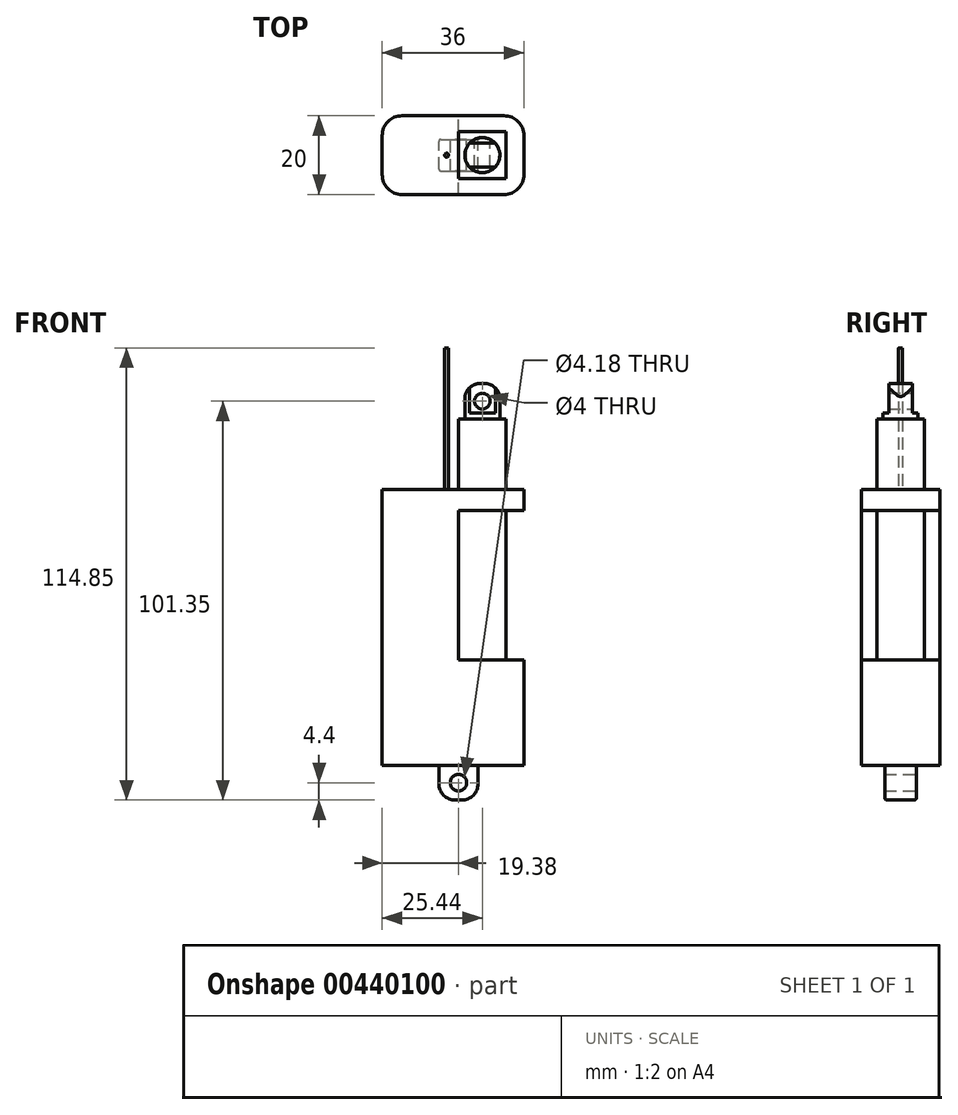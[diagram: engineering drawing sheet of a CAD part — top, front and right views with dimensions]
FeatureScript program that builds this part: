
annotation { "Feature Type Name" : "Feature", "Feature Type Description" : "" }
export const myFeature = defineFeature(function(context is Context, id is Id, definition is map)
    precondition{}
    {
        {
            var Q0;
            Q0=qCreatedBy(makeId("Front.planeOp"),FACE);
            var sketch = newSketch(context, id + "F0", { "sketchPlane" : qUnion([Q0])});
            skLineSegment(sketch, "E0", {"start": v(0, 0) * mm, "end": v(0, 70.05) * mm, "construction": true});
            skLineSegment(sketch, "E1", {"start": v(0, 0) * mm, "end": v(0, -8.8) * mm, "construction": true});
            skCircle(sketch, "E2", {"center": v(0, -4.4) * mm, "radius": 2.09 * mm});
            skLineSegment(sketch, "E3", {"start": v(-4.98, 0) * mm, "end": v(-4.98, -4.62) * mm});
            skLineSegment(sketch, "E4", {"start": v(-0.8, -8.8) * mm, "end": v(0.8, -8.8) * mm});
            skLineSegment(sketch, "E5", {"start": v(4.98, -4.62) * mm, "end": v(4.98, 0) * mm});
            skPoint(sketch, "E6.visualSharp", {"position": v(-4.98, -8.8) * mm});
            skArc(sketch, "E6.filletArc", {"start": v(-4.98, -4.62) * mm, "mid": v(-3.76, -7.58) * mm, "end": v(-0.8, -8.8) * mm});
            skPoint(sketch, "E7.visualSharp", {"position": v(4.98, -8.8) * mm});
            skArc(sketch, "E7.filletArc", {"start": v(0.8, -8.8) * mm, "mid": v(3.76, -7.58) * mm, "end": v(4.98, -4.62) * mm});
            skLineSegment(sketch, "E8", {"start": v(0, 0) * mm, "end": v(-19.38, 0) * mm});
            skLineSegment(sketch, "E9", {"start": v(4.98, 0) * mm, "end": v(16.62, 0) * mm});
            skLineSegment(sketch, "E10", {"start": v(-19.38, 0) * mm, "end": v(-19.38, 70.05) * mm});
            skLineSegment(sketch, "E11", {"start": v(16.62, 0) * mm, "end": v(16.62, 26.8) * mm});
            skLineSegment(sketch, "E12", {"start": v(16.62, 64.8) * mm, "end": v(16.62, 70.05) * mm});
            skLineSegment(sketch, "E13", {"start": v(16.62, 64.8) * mm, "end": v(12.12, 64.8) * mm});
            skLineSegment(sketch, "E14", {"start": v(12.12, 64.8) * mm, "end": v(12.12, 26.8) * mm});
            skLineSegment(sketch, "E15", {"start": v(12.12, 26.8) * mm, "end": v(16.62, 26.8) * mm});
            skLineSegment(sketch, "E16", {"start": v(16.62, 70.05) * mm, "end": v(12.12, 70.05) * mm});
            skLineSegment(sketch, "E17", {"start": v(12.12, 70.05) * mm, "end": v(12.12, 88.05) * mm});
            skLineSegment(sketch, "E18", {"start": v(12.12, 88.05) * mm, "end": v(10.56, 88.05) * mm});
            skLineSegment(sketch, "E19", {"start": v(10.56, 88.05) * mm, "end": v(10.56, 93.05) * mm});
            skLineSegment(sketch, "E20", {"start": v(6.56, 97.05) * mm, "end": v(5.56, 97.05) * mm});
            skLineSegment(sketch, "E21", {"start": v(1.56, 93.05) * mm, "end": v(1.56, 88.05) * mm});
            skLineSegment(sketch, "E22", {"start": v(1.56, 88.05) * mm, "end": v(0, 88.05) * mm});
            skLineSegment(sketch, "E23", {"start": v(0, 88.05) * mm, "end": v(0, 70.05) * mm});
            skLineSegment(sketch, "E24", {"start": v(0, 70.05) * mm, "end": v(-19.38, 70.05) * mm});
            skCircle(sketch, "E25", {"center": v(6.06, 92.55) * mm, "radius": 2 * mm});
            skPoint(sketch, "E25.centerSnap0", {"position": v(6.06, 97.05) * mm});
            skPoint(sketch, "E25.centerSnap1", {"position": v(1.56, 92.55) * mm});
            skPoint(sketch, "E26.visualSharp", {"position": v(10.56, 97.05) * mm});
            skArc(sketch, "E26.filletArc", {"start": v(10.56, 93.05) * mm, "mid": v(9.39, 95.88) * mm, "end": v(6.56, 97.05) * mm});
            skPoint(sketch, "E27.visualSharp", {"position": v(1.56, 97.05) * mm});
            skArc(sketch, "E27.filletArc", {"start": v(5.56, 97.05) * mm, "mid": v(2.73, 95.88) * mm, "end": v(1.56, 93.05) * mm});
            skLineSegment(sketch, "E28", {"start": v(1.56, 88.05) * mm, "end": v(10.56, 88.05) * mm});
            skLineSegment(sketch, "E29", {"start": v(1.56, 89.55) * mm, "end": v(10.56, 89.55) * mm});
            skLineSegment(sketch, "E30", {"start": v(0, 70.05) * mm, "end": v(12.12, 70.05) * mm});
            skLineSegment(sketch, "E31", {"start": v(0, 0) * mm, "end": v(4.98, 0) * mm});
            skLineSegment(sketch, "E32", {"start": v(12.12, 64.8) * mm, "end": v(0, 64.8) * mm});
            skLineSegment(sketch, "E33", {"start": v(0, 64.8) * mm, "end": v(0, 26.8) * mm});
            skLineSegment(sketch, "E34", {"start": v(0, 26.8) * mm, "end": v(12.12, 26.8) * mm});
            skLineSegment(sketch, "E35", {"start": v(-3, 70.05) * mm, "end": v(-3, 106.05) * mm});
            skSolve(sketch);
        }
        {
            var Q0;
            Q0=makeQuery(id+"F0.imprint","IMPRINT",FACE,{"disambiguationData":[TD([[makeQuery(id+"F0.imprint","IMPRINT",EDGE,{"derivedFrom":sQuery(id+"F0.wireOp",EDGE,"E9")}),1.0]])]});
            extrude(context, id + "F1", {"entities" : qUnion([Q0]), "endBound" : BoundingType.SYMMETRIC, "depth" : 20 * mm, "offsetDistance" : 25 * mm});
        }
        {
            var Q0;
            Q0=makeQuery(id+"F0.imprint","IMPRINT",FACE,{"disambiguationData":[TD([[makeQuery(id+"F0.imprint","IMPRINT",EDGE,{"derivedFrom":sQuery(id+"F0.wireOp",EDGE,"E2")}),-1.0]])]});
            extrude(context, id + "F2", {"entities" : qUnion([Q0]), "operationType" : NewBodyOperationType.ADD, "endBound" : BoundingType.SYMMETRIC, "depth" : 8 * mm, "offsetDistance" : 25 * mm});
        }
        {
            var Q0;
            Q0=makeQuery(id+"F0.imprint","IMPRINT",FACE,{"disambiguationData":[TD([[makeQuery(id+"F0.imprint","IMPRINT",EDGE,{"derivedFrom":sQuery(id+"F0.wireOp",EDGE,"E17")}),1.0]])]});
            extrude(context, id + "F3", {"entities" : qUnion([Q0]), "operationType" : NewBodyOperationType.ADD, "endBound" : BoundingType.SYMMETRIC, "depth" : 12 * mm, "offsetDistance" : 25 * mm});
        }
        {
            var Q0;
            Q0=makeQuery(id+"F0.imprint","IMPRINT",FACE,{"disambiguationData":[TD([[makeQuery(id+"F0.imprint","IMPRINT",EDGE,{"derivedFrom":sQuery(id+"F0.wireOp",EDGE,"E14")}),-1.0]])]});
            extrude(context, id + "F4", {"entities" : qUnion([Q0]), "operationType" : NewBodyOperationType.ADD, "endBound" : BoundingType.SYMMETRIC, "depth" : 12 * mm, "offsetDistance" : 25 * mm});
        }
        {
            var Q0;
            Q0=makeQuery(id+"F1.opExtrude","SWEPT_FACE",FACE,{"disambiguationData":[OSD([sQuery(id+"F0.wireOp",EDGE,"E16"),sQuery(id+"F0.wireOp",EDGE,"E24"),sQuery(id+"F0.wireOp",EDGE,"E30")])]});
            var Q1;
            Q1=sQuery(id+"F0.wireOp",VERTEX,"E35.start");
            cPlane(context, id + "F5", {"entities" : qUnion([Q0, Q1]), "cplaneType" : CPlaneType.PLANE_POINT, "offset" : 25 * mm, "width" : 150 * mm, "height" : 150 * mm});
        }
        {
            var Q0;
            Q0=qCreatedBy(id+"F5.planeOp",FACE);
            var sketch = newSketch(context, id + "F6", { "sketchPlane" : qUnion([Q0])});
            skLineSegment(sketch, "E36", {"start": v(0, 0) * mm, "end": v(-3, 0) * mm, "construction": true});
            skCircle(sketch, "E37", {"center": v(-3, 0) * mm, "radius": 0.5 * mm});
            skSolve(sketch);
        }
        {
            var Q0;
            Q0=makeQuery(id+"F6.imprint","IMPRINT",FACE,{"disambiguationData":[TD([[makeQuery(id+"F6.imprint","IMPRINT",EDGE,{"derivedFrom":sQuery(id+"F6.wireOp",EDGE,"E37")}),1.0]])]});
            extrude(context, id + "F7", {"entities" : qUnion([Q0]), "operationType" : NewBodyOperationType.ADD, "depth" : 36 * mm, "offsetDistance" : 25 * mm});
        }
        {
            var Q0;
            Q0=makeQuery(id+"F1.opExtrude","CAP_EDGE",EDGE,{"disambiguationData":[OSD([sQuery(id+"F0.wireOp",EDGE,"E10")])],"isStart":true});
            var Q1;
            Q1=makeQuery(id+"F1.opExtrude","CAP_EDGE",EDGE,{"disambiguationData":[OSD([sQuery(id+"F0.wireOp",EDGE,"E10")])],"isStart":false});
            var Q2;
            Q2=makeQuery(id+"F1.opExtrude","CAP_EDGE",EDGE,{"disambiguationData":[OSD([sQuery(id+"F0.wireOp",EDGE,"E11")])],"isStart":true});
            var Q3;
            Q3=makeQuery(id+"F1.opExtrude","CAP_EDGE",EDGE,{"disambiguationData":[OSD([sQuery(id+"F0.wireOp",EDGE,"E11")])],"isStart":false});
            var Q4;
            Q4=makeQuery(id+"F1.opExtrude","CAP_EDGE",EDGE,{"disambiguationData":[OSD([sQuery(id+"F0.wireOp",EDGE,"E12")])],"isStart":true});
            var Q5;
            Q5=makeQuery(id+"F1.opExtrude","CAP_EDGE",EDGE,{"disambiguationData":[OSD([sQuery(id+"F0.wireOp",EDGE,"E12")])],"isStart":false});
            fillet(context, id + "F8", {"entities" : qUnion([Q0, Q1, Q2, Q3, Q4, Q5]), "radius" : 5 * mm, "tangentPropagation" : true, "allowEdgeOverflow" : false});
        }
        {
            var Q0;
            Q0=makeQuery(id+"F3.opExtrude","SWEPT_FACE",FACE,{"disambiguationData":[OSD([sQuery(id+"F0.wireOp",EDGE,"E18"),sQuery(id+"F0.wireOp",EDGE,"E22"),sQuery(id+"F0.wireOp",EDGE,"E28")])]});
            cPlane(context, id + "F9", {"entities" : qUnion([Q0]), "cplaneType" : CPlaneType.OFFSET, "offset" : 0 * mm, "width" : 150 * mm, "height" : 150 * mm});
        }
        {
            var Q0;
            Q0=qCreatedBy(id+"F9.planeOp",FACE);
            var sketch = newSketch(context, id + "F10", { "sketchPlane" : qUnion([Q0])});
            skLineSegment(sketch, "E38", {"start": v(0, 0) * mm, "end": v(6.06, 0) * mm, "construction": true});
            skCircle(sketch, "E39", {"center": v(6.06, 0) * mm, "radius": 4.45 * mm});
            skSolve(sketch);
        }
        {
            var Q0;
            Q0=makeQuery(id+"F10.imprint","IMPRINT",FACE,{"disambiguationData":[TD([[makeQuery(id+"F10.imprint","IMPRINT",EDGE,{"derivedFrom":sQuery(id+"F10.wireOp",EDGE,"E39")}),1.0]])]});
            extrude(context, id + "F11", {"entities" : qUnion([Q0]), "operationType" : NewBodyOperationType.ADD, "depth" : 1.5 * mm, "offsetDistance" : 25 * mm});
        }
        {
            var Q0;
            Q0=makeQuery(id+"F0.imprint","IMPRINT",FACE,{"disambiguationData":[TD([[makeQuery(id+"F0.imprint","IMPRINT",EDGE,{"derivedFrom":sQuery(id+"F0.wireOp",EDGE,"E20")}),1.0]])]});
            extrude(context, id + "F12", {"entities" : qUnion([Q0]), "operationType" : NewBodyOperationType.ADD, "endBound" : BoundingType.SYMMETRIC, "depth" : 6 * mm, "offsetDistance" : 25 * mm});
        }
        {
            var Q0;
            Q0=makeQuery(id+"F3.opExtrude","SWEPT_FACE",FACE,{"disambiguationData":[OSD([sQuery(id+"F0.wireOp",EDGE,"E18"),sQuery(id+"F0.wireOp",EDGE,"E22"),sQuery(id+"F0.wireOp",EDGE,"E28")])]});
            extrude(context, id + "F13", {"entities" : qUnion([Q0]), "operationType" : NewBodyOperationType.REMOVE, "depth" : 25 * mm, "offsetDistance" : 25 * mm});
        }
        {
            var Q0;
            Q0=makeQuery(id+"F2.opExtrude","CAP_EDGE",EDGE,{"disambiguationData":[OSD([sQuery(id+"F0.wireOp",EDGE,"E5")])],"isStart":false});
            var Q1;
            Q1=makeQuery(id+"F2.opExtrude","CAP_EDGE",EDGE,{"disambiguationData":[OSD([sQuery(id+"F0.wireOp",EDGE,"E5")])],"isStart":true});
            var Q2;
            Q2=makeQuery(id+"F2.opExtrude","CAP_EDGE",EDGE,{"disambiguationData":[OSD([sQuery(id+"F0.wireOp",EDGE,"E3")])],"isStart":false});
            var Q3;
            Q3=makeQuery(id+"F2.opExtrude","CAP_EDGE",EDGE,{"disambiguationData":[OSD([sQuery(id+"F0.wireOp",EDGE,"E3")])],"isStart":true});
            fillet(context, id + "F14", {"entities" : qUnion([Q0, Q1, Q2, Q3]), "radius" : .5 * mm, "tangentPropagation" : true, "allowEdgeOverflow" : false});
        }
    });
